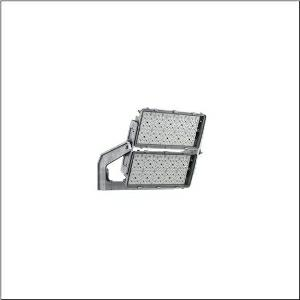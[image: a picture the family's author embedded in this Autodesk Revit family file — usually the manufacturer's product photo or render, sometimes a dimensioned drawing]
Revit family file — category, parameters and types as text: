
# Revit family: floodlight_fl_11_maxi_remote___rs07_5xa779514k01aa_47cf
name_source: partatom
category: Lighting Fixtures
units: mm (PartAtom-declared; Revit-internal decimal feet)

## family parameters
Cut with Voids When Loaded = No
Host = Face
Light Source = No
Part Type = Normal
Room Calculation Point = No
Round Connector Dimension = Use Diameter
Shared = No

## types (1)
- --- (1 x LED, 88570 lm, 916.8 W, 5700K)
    Apparent Load = 917 VA
    CIE Flux Codes = 80 93 99 100 99
    Color Rendering = 90
    Color Temperature = 5700K
    Default Elevation = 1800 mm
    Description = Floodlight FL 11  maxi  Remote floodlight; light control with lens of PMMA; cover panel of toughened safety glass, transparent; light distribution: RS07, rotationally symmetric direct distribution, LEDcolour temperature: 5700K, rated luminous flux: 88.570lm, colour rendering: CRI > 90, light colour: 957; luminous efficacy: 97lm/W; brightness control: DMX+RDM; with terminal, 6-pole, max. 2.5mm², mains connection: 220..240V/380..400V AC, 50/60Hz, surge voltage resistance: line to ground: 10kV, ECG replaceable separately, no afterglow with DALI off / DMX off command, LED unit replaceable without ESD environment, dustproof LED module, dimming range 10..100%; 917W floodlight with 2x LED unit of diecast aluminium, coated grey; length: 713mm / width: 651mm / height: 338mm; housing frame, of diecast aluminium, uncoated, natural, mounting bracket, of diecast aluminium, uncoated, natural, equipment: Power, protection rating (complete): IP66; insulation class (complete): insulation class I (protective earthing); certification: CE, ENEC, VDE; ball protection: ball impact resistance with accessories, rated ambient temperature 10°C, only for outdoor installations, permissible operating ambient temperature: -40..+30°C, permissible storage temperature: -40..+85°C; packaging unit: 1 piece

Light Distribution: RS07
    Height = 320 mm
    Lamp = 1 x LED
    Lamp Light Flux = 88570 lm
    Lamp Power = 916.8 W
    Lamp count = 1
    Length = 712 mm
    Luminous efficacy = 97 lm/W
    Manufacturer = Siteco
    ModVariant = No
    Model = 5XA779514K01AA
    Number of Poles = 1
    OnlyDefault = Yes
    Power Factor = 1
    Product Name = Floodlight FL 11 maxi Remote | RS07
    Product group = floodlight | pylon top
    ProductGroupID = 6101
    Protection Class = Protection class I
    Protection Degree = IP 66
    RLX_Detail_Level = 1
    RlxData = <blob elided: 41073 chars, md5=e79a64f5>
    Socket = socket
    Standby Power = 0 W
    System Light Flux = 88570 lm
    System Power = 917 W
    Type Comments = factory setting: luminous flux: 100 % | dim-lin: 254 | 950 mA
    Type Image = l_1006788.jpg
    URL = http://relux.com
    VarID = @adj_095091
    Voltage = 0 V
    Weight = 0.00 kg
    Width = 655 mm

## geometry (parser evidence)
native form markers: Blend x4, Sweep x13
no freeform markers — native parametric forms only
